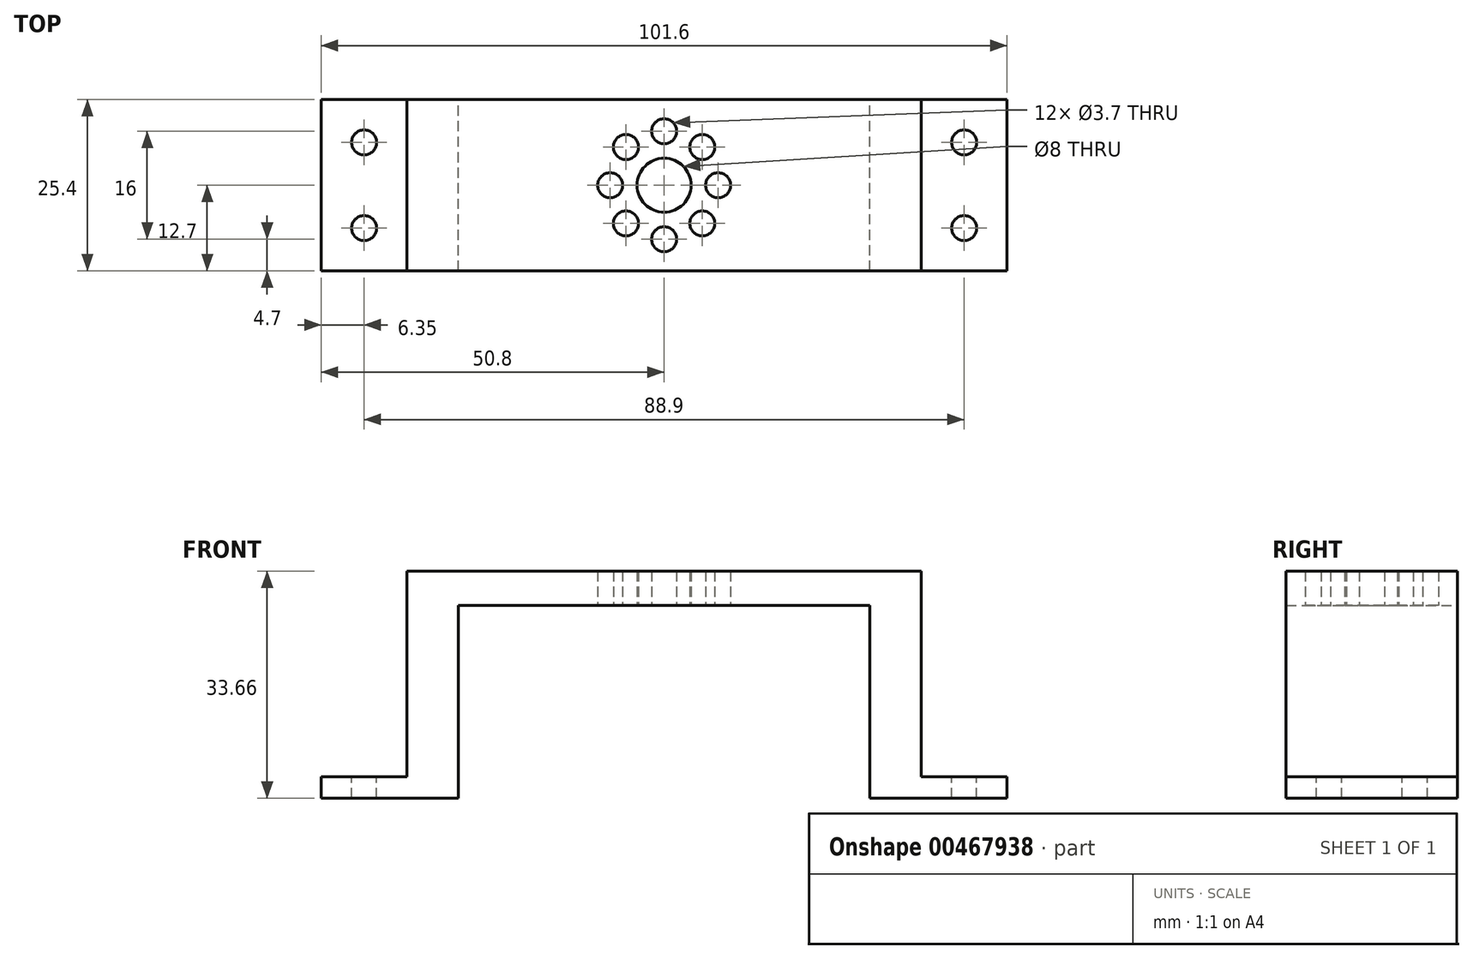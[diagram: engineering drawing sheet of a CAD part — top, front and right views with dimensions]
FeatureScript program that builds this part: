
annotation { "Feature Type Name" : "Feature", "Feature Type Description" : "" }
export const myFeature = defineFeature(function(context is Context, id is Id, definition is map)
    precondition{}
    {
        {
            var Q0;
            Q0=qCreatedBy(makeId("Top.planeOp"),FACE);
            var sketch = newSketch(context, id + "F0", { "sketchPlane" : qUnion([Q0])});
            skLineSegment(sketch, "E0.bottom", {"start": v(-38.1, 12.7) * mm, "end": v(38.1, 12.7) * mm});
            skLineSegment(sketch, "E0.top", {"start": v(-38.1, -12.7) * mm, "end": v(38.1, -12.7) * mm});
            skLineSegment(sketch, "E0.left", {"start": v(-38.1, 12.7) * mm, "end": v(-38.1, -12.7) * mm});
            skLineSegment(sketch, "E0.right", {"start": v(38.1, 12.7) * mm, "end": v(38.1, -12.7) * mm});
            skPoint(sketch, "E0.middle", {"position": v(0, 0) * mm});
            skCircle(sketch, "E1", {"center": v(0, 0) * mm, "radius": 4 * mm});
            skCircle(sketch, "E2", {"center": v(0, 8) * mm, "radius": 1.85 * mm});
            skCircle(sketch, "E3.1.0", {"center": v(-5.66, 5.66) * mm, "radius": 1.85 * mm});
            skCircle(sketch, "E3.2.0", {"center": v(-8, 0) * mm, "radius": 1.85 * mm});
            skCircle(sketch, "E3.3.0", {"center": v(-5.66, -5.66) * mm, "radius": 1.85 * mm});
            skCircle(sketch, "E3.4.0", {"center": v(0, -8) * mm, "radius": 1.85 * mm});
            skCircle(sketch, "E3.5.0", {"center": v(5.66, -5.66) * mm, "radius": 1.85 * mm});
            skCircle(sketch, "E3.6.0", {"center": v(8, 0) * mm, "radius": 1.85 * mm});
            skCircle(sketch, "E3.7.0", {"center": v(5.66, 5.66) * mm, "radius": 1.85 * mm});
            skSolve(sketch);
        }
        {
            var Q0;
            Q0 = qSketchRegion(id + "F0", true);
            extrude(context, id + "F1", {"entities" : qUnion([Q0]), "depth" : 5.08 * mm});
        }
        {
            var Q0;
            Q0=makeQuery(id+"F1.opExtrude","CAP_FACE",FACE,{"disambiguationData":[OSD([sQuery(id+"F0.wireOp",EDGE,"E0.bottom"),sQuery(id+"F0.wireOp",EDGE,"E0.top"),sQuery(id+"F0.wireOp",EDGE,"E0.left"),sQuery(id+"F0.wireOp",EDGE,"E0.right")])],"isStart":true});
            var sketch = newSketch(context, id + "F2", { "sketchPlane" : qUnion([Q0])});
            skLineSegment(sketch, "E4.bottom", {"start": v(-38.1, 12.7) * mm, "end": v(-30.48, 12.7) * mm});
            skLineSegment(sketch, "E4.top", {"start": v(-38.1, -12.7) * mm, "end": v(-30.48, -12.7) * mm});
            skLineSegment(sketch, "E4.left", {"start": v(-38.1, 12.7) * mm, "end": v(-38.1, -12.7) * mm});
            skLineSegment(sketch, "E4.right", {"start": v(-30.48, 12.7) * mm, "end": v(-30.48, -12.7) * mm});
            skLineSegment(sketch, "E5.bottom", {"start": v(38.1, 12.7) * mm, "end": v(30.48, 12.7) * mm});
            skLineSegment(sketch, "E5.top", {"start": v(38.1, -12.7) * mm, "end": v(30.48, -12.7) * mm});
            skLineSegment(sketch, "E5.left", {"start": v(38.1, 12.7) * mm, "end": v(38.1, -12.7) * mm});
            skLineSegment(sketch, "E5.right", {"start": v(30.48, 12.7) * mm, "end": v(30.48, -12.7) * mm});
            skSolve(sketch);
        }
        {
            var Q0;
            Q0=makeQuery(id+"F2.imprint","IMPRINT",FACE,{"disambiguationData":[TD([[makeQuery(id+"F2.imprint","IMPRINT",EDGE,{"derivedFrom":sQuery(id+"F2.wireOp",EDGE,"E5.bottom")}),-1.0]])]});
            var Q1;
            Q1=makeQuery(id+"F2.imprint","IMPRINT",FACE,{"disambiguationData":[TD([[makeQuery(id+"F2.imprint","IMPRINT",EDGE,{"derivedFrom":sQuery(id+"F2.wireOp",EDGE,"E4.bottom")}),-1.0]])]});
            extrude(context, id + "F3", {"entities" : qUnion([Q0, Q1]), "operationType" : NewBodyOperationType.ADD, "depth" : 25.4 * mm});
        }
        {
            var Q0;
            Q0=makeQuery(id+"F3.opExtrude","CAP_FACE",FACE,{"disambiguationData":[OSD([sQuery(id+"F2.wireOp",EDGE,"E4.bottom"),sQuery(id+"F2.wireOp",EDGE,"E4.top"),sQuery(id+"F2.wireOp",EDGE,"E4.left"),sQuery(id+"F2.wireOp",EDGE,"E4.right")])],"isStart":false});
            var sketch = newSketch(context, id + "F4", { "sketchPlane" : qUnion([Q0])});
            skLineSegment(sketch, "E6.bottom", {"start": v(-30.48, 12.7) * mm, "end": v(-50.8, 12.7) * mm});
            skLineSegment(sketch, "E6.top", {"start": v(-30.48, -12.7) * mm, "end": v(-50.8, -12.7) * mm});
            skLineSegment(sketch, "E6.left", {"start": v(-30.48, 12.7) * mm, "end": v(-30.48, -12.7) * mm});
            skLineSegment(sketch, "E6.right", {"start": v(-50.8, 12.7) * mm, "end": v(-50.8, -12.7) * mm});
            skLineSegment(sketch, "E7.bottom", {"start": v(30.48, 12.7) * mm, "end": v(50.8, 12.7) * mm});
            skLineSegment(sketch, "E7.top", {"start": v(30.48, -12.7) * mm, "end": v(50.8, -12.7) * mm});
            skLineSegment(sketch, "E7.left", {"start": v(30.48, 12.7) * mm, "end": v(30.48, -12.7) * mm});
            skLineSegment(sketch, "E7.right", {"start": v(50.8, 12.7) * mm, "end": v(50.8, -12.7) * mm});
            skPoint(sketch, "E8", {"position": v(-38.1, 12.7) * mm});
            skCircle(sketch, "E9", {"center": v(-44.45, 6.35) * mm, "radius": 1.85 * mm});
            skCircle(sketch, "E10", {"center": v(-44.45, -6.35) * mm, "radius": 1.85 * mm});
            skPoint(sketch, "E11.orphan", {"position": v(-44.45, 12.7) * mm});
            skLineSegment(sketch, "E12", {"start": v(0, 12.7) * mm, "end": v(0, -12.7) * mm});
            skCircle(sketch, "E13.MirrorC", {"center": v(44.45, 6.35) * mm, "radius": 1.85 * mm});
            skCircle(sketch, "E14.MirrorC", {"center": v(44.45, -6.35) * mm, "radius": 1.85 * mm});
            skSolve(sketch);
        }
        {
            var Q0;
            {var subQ2=sQuery(id+"F4.wireOp",EDGE,"E6.right");Q0=makeQuery(id+"F4.imprint","IMPRINT",FACE,{"disambiguationData":[TD([[makeQuery(id+"F4.imprint","IMPRINT",EDGE,{"derivedFrom":subQ2}),1.0]])]});}
            var Q1;
            {var subQ2=sQuery(id+"F4.wireOp",EDGE,"E6.left");Q1=makeQuery(id+"F4.imprint","IMPRINT",FACE,{"disambiguationData":[TD([[makeQuery(id+"F4.imprint","IMPRINT",EDGE,{"derivedFrom":subQ2}),-1.0]])]});}
            var Q2;
            Q2=makeQuery(id+"F4.imprint","IMPRINT",FACE,{"disambiguationData":[TD([[makeQuery(id+"F4.imprint","IMPRINT",EDGE,{"derivedFrom":sQuery(id+"F4.wireOp",EDGE,"E7.bottom")}),-1.0]])]});
            extrude(context, id + "F5", {"entities" : qUnion([Q0, Q1, Q2]), "operationType" : NewBodyOperationType.ADD, "depth" : 3.17 * mm});
        }
    });
